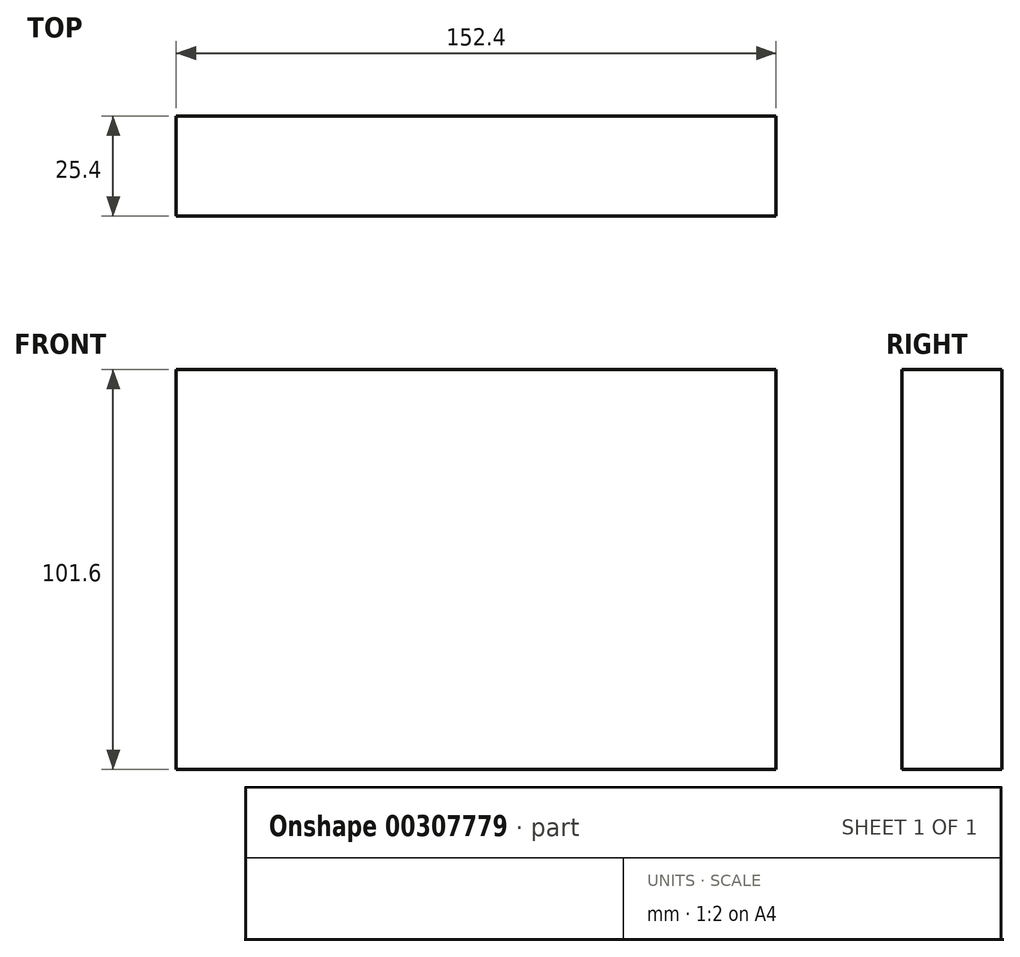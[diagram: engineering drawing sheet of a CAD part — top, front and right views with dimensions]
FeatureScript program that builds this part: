
annotation { "Feature Type Name" : "Feature", "Feature Type Description" : "" }
export const myFeature = defineFeature(function(context is Context, id is Id, definition is map)
    precondition{}
    {
        {
            var Q0;
            Q0=qCreatedBy(makeId("Front.planeOp"),FACE);
            var sketch = newSketch(context, id + "F0", { "sketchPlane" : qUnion([Q0])});
            skLineSegment(sketch, "E0.bottom", {"start": v(-75.43, 62.29) * mm, "end": v(76.97, 62.29) * mm});
            skLineSegment(sketch, "E0.top", {"start": v(-75.43, -39.31) * mm, "end": v(76.97, -39.31) * mm});
            skLineSegment(sketch, "E0.left", {"start": v(-75.43, 62.29) * mm, "end": v(-75.43, -39.31) * mm});
            skLineSegment(sketch, "E0.right", {"start": v(76.97, 62.29) * mm, "end": v(76.97, -39.31) * mm});
            skLineSegment(sketch, "E1", {"start": v(51.57, 62.29) * mm, "end": v(51.57, -39.31) * mm});
            skLineSegment(sketch, "E2", {"start": v(-50.03, 62.29) * mm, "end": v(-50.03, -39.31) * mm});
            skLineSegment(sketch, "E3", {"start": v(-50.03, 36.89) * mm, "end": v(51.57, 36.89) * mm});
            skLineSegment(sketch, "E4", {"start": v(51.57, -13.91) * mm, "end": v(-50.03, -13.91) * mm});
            skSolve(sketch);
        }
        {
            var Q0;
            Q0=makeQuery(id+"F0.imprint","IMPRINT",FACE,{"disambiguationData":[TD([[makeQuery(id+"F0.imprint","IMPRINT",EDGE,{"derivedFrom":sQuery(id+"F0.wireOp",EDGE,"E0.bottom")}),-1.0]])]});
            extrude(context, id + "F1", {"entities" : qUnion([Q0]), "depth" : 25.4 * mm});
        }
        {
            var Q0;
            {var subQ4=sQuery(id+"F0.wireOp",EDGE,"E0.left");Q0=makeQuery(id+"F0.imprint","IMPRINT",FACE,{"disambiguationData":[TD([[makeQuery(id+"F0.imprint","IMPRINT",EDGE,{"derivedFrom":subQ4}),1.0]])]});}
            var Q1;
            {var subQ0=sQuery(id+"F0.wireOp",EDGE,"E3");Q1=makeQuery(id+"F0.imprint","IMPRINT",FACE,{"disambiguationData":[TD([[makeQuery(id+"F0.imprint","IMPRINT",EDGE,{"derivedFrom":subQ0}),-1.0]])]});}
            var Q2;
            {var subQ5=sQuery(id+"F0.wireOp",EDGE,"E4");Q2=makeQuery(id+"F0.imprint","IMPRINT",FACE,{"disambiguationData":[TD([[makeQuery(id+"F0.imprint","IMPRINT",EDGE,{"derivedFrom":subQ5}),1.0]])]});}
            var Q3;
            {var subQ4=sQuery(id+"F0.wireOp",EDGE,"E0.right");Q3=makeQuery(id+"F0.imprint","IMPRINT",FACE,{"disambiguationData":[TD([[makeQuery(id+"F0.imprint","IMPRINT",EDGE,{"derivedFrom":subQ4}),-1.0]])]});}
            extrude(context, id + "F2", {"entities" : qUnion([Q0, Q1, Q2, Q3]), "operationType" : NewBodyOperationType.ADD, "depth" : 25.4 * mm});
        }
    });
